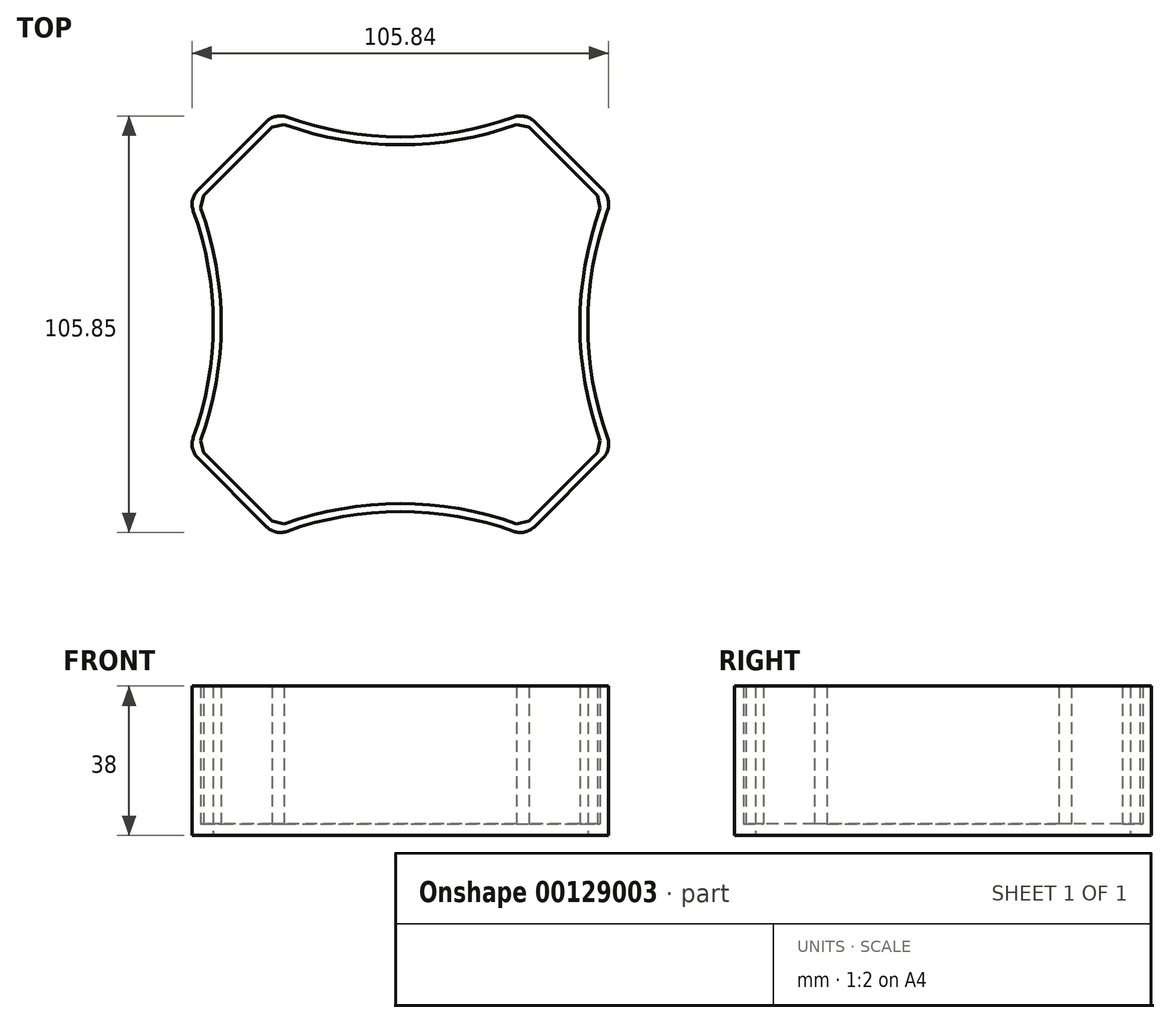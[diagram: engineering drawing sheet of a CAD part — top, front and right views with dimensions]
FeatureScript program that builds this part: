
annotation { "Feature Type Name" : "Feature", "Feature Type Description" : "" }
export const myFeature = defineFeature(function(context is Context, id is Id, definition is map)
    precondition{}
    {
        {
            var Q0;
            Q0=qCreatedBy(makeId("Top.planeOp"),FACE);
            var sketch = newSketch(context, id + "F0", { "sketchPlane" : qUnion([Q0])});
            skPoint(sketch, "E0.middle", {"position": v(0, 0) * mm});
            skLineSegment(sketch, "E1", {"start": v(34.04, 51.46) * mm, "end": v(51.46, 34.04) * mm});
            skLineSegment(sketch, "E2", {"start": v(-34.04, 51.46) * mm, "end": v(-51.45, 34.05) * mm});
            skLineSegment(sketch, "E3", {"start": v(-51.45, -34.05) * mm, "end": v(-34.04, -51.46) * mm});
            skLineSegment(sketch, "E4", {"start": v(51.46, -34.04) * mm, "end": v(34.04, -51.46) * mm});
            skArc(sketch, "E5", {"start": v(52.63, 28.81) * mm, "mid": v(47.62, 0) * mm, "end": v(52.63, -28.81) * mm});
            skArc(sketch, "E6", {"start": v(-28.8, 52.62) * mm, "mid": v(0, 47.58) * mm, "end": v(28.8, 52.62) * mm});
            skArc(sketch, "E7", {"start": v(-52.61, -28.8) * mm, "mid": v(-47.52, 0) * mm, "end": v(-52.61, 28.8) * mm});
            skArc(sketch, "E8", {"start": v(28.81, -52.63) * mm, "mid": v(0, -47.6) * mm, "end": v(-28.8, -52.63) * mm});
            skPoint(sketch, "E9.visualSharp", {"position": v(-31.75, 53.75) * mm});
            skArc(sketch, "E9.filletArc", {"start": v(-28.8, 52.62) * mm, "mid": v(-31.6, 52.8) * mm, "end": v(-34.04, 51.46) * mm});
            skPoint(sketch, "E10.visualSharp", {"position": v(-53.75, 31.75) * mm});
            skArc(sketch, "E10.filletArc", {"start": v(-51.45, 34.05) * mm, "mid": v(-52.8, 31.6) * mm, "end": v(-52.61, 28.8) * mm});
            skPoint(sketch, "E11.visualSharp", {"position": v(31.75, 53.75) * mm});
            skArc(sketch, "E11.filletArc", {"start": v(34.04, 51.46) * mm, "mid": v(31.6, 52.8) * mm, "end": v(28.8, 52.62) * mm});
            skPoint(sketch, "E12.visualSharp", {"position": v(53.75, 31.75) * mm});
            skArc(sketch, "E12.filletArc", {"start": v(52.63, 28.81) * mm, "mid": v(52.8, 31.6) * mm, "end": v(51.46, 34.04) * mm});
            skPoint(sketch, "E13.visualSharp", {"position": v(53.75, -31.75) * mm});
            skArc(sketch, "E13.filletArc", {"start": v(51.46, -34.04) * mm, "mid": v(52.8, -31.6) * mm, "end": v(52.63, -28.81) * mm});
            skPoint(sketch, "E14.visualSharp", {"position": v(31.75, -53.75) * mm});
            skArc(sketch, "E14.filletArc", {"start": v(28.81, -52.63) * mm, "mid": v(31.6, -52.8) * mm, "end": v(34.04, -51.46) * mm});
            skPoint(sketch, "E15.visualSharp", {"position": v(-31.75, -53.75) * mm});
            skArc(sketch, "E15.filletArc", {"start": v(-34.04, -51.46) * mm, "mid": v(-31.6, -52.8) * mm, "end": v(-28.8, -52.63) * mm});
            skPoint(sketch, "E16.visualSharp", {"position": v(-53.75, -31.75) * mm});
            skArc(sketch, "E16.filletArc", {"start": v(-52.61, -28.8) * mm, "mid": v(-52.8, -31.6) * mm, "end": v(-51.45, -34.05) * mm});
            skLineSegment(sketch, "E17.0", {"start": v(-32.63, 50.04) * mm, "end": v(-50.04, 32.64) * mm});
            skArc(sketch, "E18.0", {"start": v(-29.49, 50.74) * mm, "mid": v(0, 45.58) * mm, "end": v(29.49, 50.74) * mm});
            skLineSegment(sketch, "E19.0", {"start": v(32.63, 50.04) * mm, "end": v(50.05, 32.62) * mm});
            skArc(sketch, "E20.0", {"start": v(50.75, 29.49) * mm, "mid": v(45.62, 0) * mm, "end": v(50.75, -29.5) * mm});
            skArc(sketch, "E21.0", {"start": v(-50.73, -29.49) * mm, "mid": v(-45.52, 0) * mm, "end": v(-50.73, 29.49) * mm});
            skLineSegment(sketch, "E22.0", {"start": v(-50.04, -32.64) * mm, "end": v(-32.62, -50.05) * mm});
            skArc(sketch, "E23.0", {"start": v(29.49, -50.75) * mm, "mid": v(0, -45.6) * mm, "end": v(-29.49, -50.75) * mm});
            skLineSegment(sketch, "E24.0", {"start": v(50.04, -32.63) * mm, "end": v(32.63, -50.05) * mm});
            skLineSegment(sketch, "E25", {"start": v(-32.63, 50.04) * mm, "end": v(-29.49, 50.74) * mm});
            skLineSegment(sketch, "E26", {"start": v(-50.04, 32.64) * mm, "end": v(-50.73, 29.49) * mm});
            skLineSegment(sketch, "E27", {"start": v(-50.73, -29.49) * mm, "end": v(-50.04, -32.64) * mm});
            skLineSegment(sketch, "E28", {"start": v(29.49, -50.75) * mm, "end": v(32.63, -50.05) * mm});
            skLineSegment(sketch, "E29", {"start": v(29.49, 50.74) * mm, "end": v(32.63, 50.04) * mm});
            skLineSegment(sketch, "E30", {"start": v(50.05, 32.62) * mm, "end": v(50.75, 29.49) * mm});
            skLineSegment(sketch, "E31", {"start": v(50.75, -29.5) * mm, "end": v(50.04, -32.63) * mm});
            skLineSegment(sketch, "E32", {"start": v(-29.49, -50.75) * mm, "end": v(-32.62, -50.05) * mm});
            skSolve(sketch);
        }
        {
            var Q0;
            Q0=makeQuery(id+"F0.imprint","IMPRINT",FACE,{"disambiguationData":[TD([[makeQuery(id+"F0.imprint","IMPRINT",EDGE,{"derivedFrom":sQuery(id+"F0.wireOp",EDGE,"E17.0")}),1.0]])]});
            extrude(context, id + "F1", {"entities" : qUnion([Q0]), "depth" : 3 * mm});
        }
        {
            var Q0;
            Q0 = qSketchRegion(id + "F0", true);
            extrude(context, id + "F2", {"entities" : qUnion([Q0]), "operationType" : NewBodyOperationType.ADD, "depth" : 38 * mm});
        }
    });
